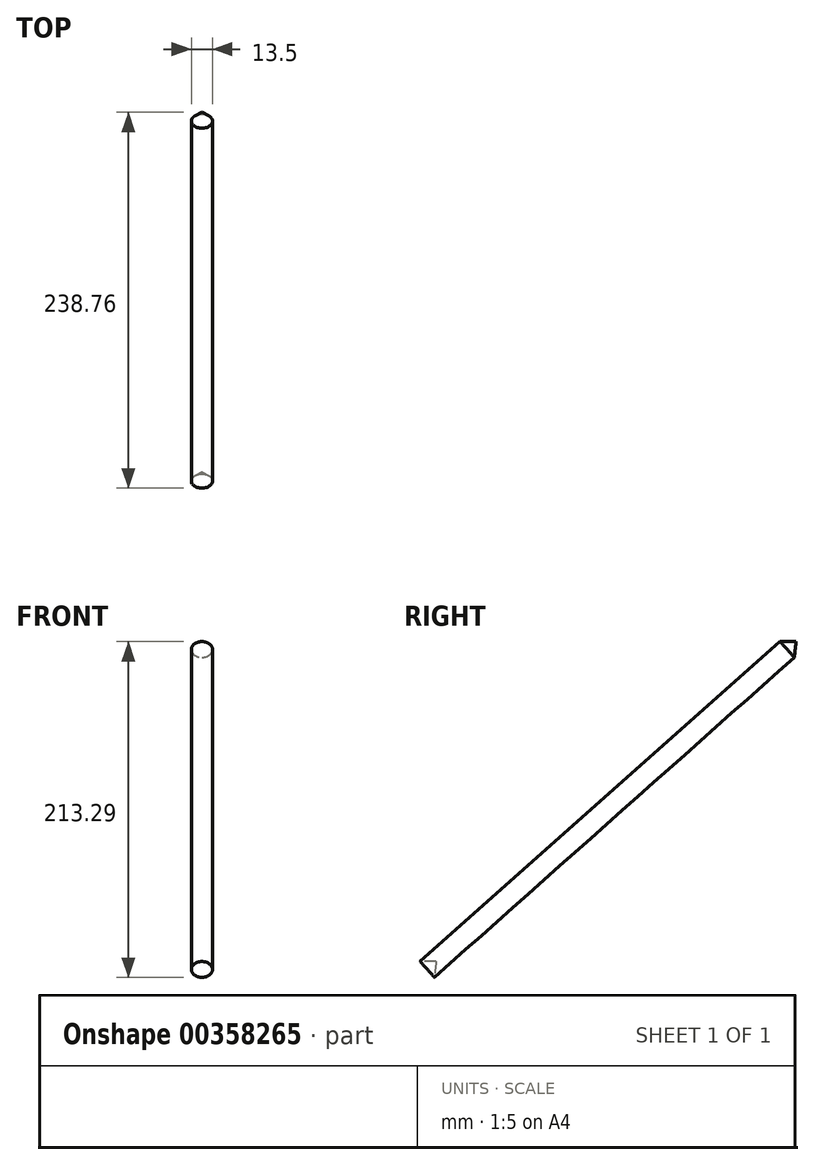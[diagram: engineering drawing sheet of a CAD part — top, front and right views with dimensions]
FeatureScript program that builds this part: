
annotation { "Feature Type Name" : "Feature", "Feature Type Description" : "" }
export const myFeature = defineFeature(function(context is Context, id is Id, definition is map)
    precondition{}
    {
        {
            var Q0;
            Q0=qCreatedBy(makeId("Right.planeOp"),FACE);
            var sketch = newSketch(context, id + "F0", { "sketchPlane" : qUnion([Q0])});
            skLineSegment(sketch, "E0", {"start": v(0, 0) * mm, "end": v(228.6, 203.2) * mm});
            skLineSegment(sketch, "E1", {"start": v(228.6, 203.2) * mm, "end": v(218.44, 203.2) * mm});
            skLineSegment(sketch, "E2", {"start": v(218.44, 203.2) * mm, "end": v(-10.16, 0) * mm});
            skLineSegment(sketch, "E3", {"start": v(-10.16, 0) * mm, "end": v(0, 0) * mm});
            skSolve(sketch);
        }
        {
            var Q0;
            Q0 = qSketchRegion(id + "F0", true);
            var Q1;
            Q1=sQuery(id+"F0.wireOp",EDGE,"E0");
            revolve(context, id + "F1", {"entities" : qUnion([Q0]), "axis" : qUnion([Q1]), "revolveType" : RevolveType.FULL});
        }
    });
